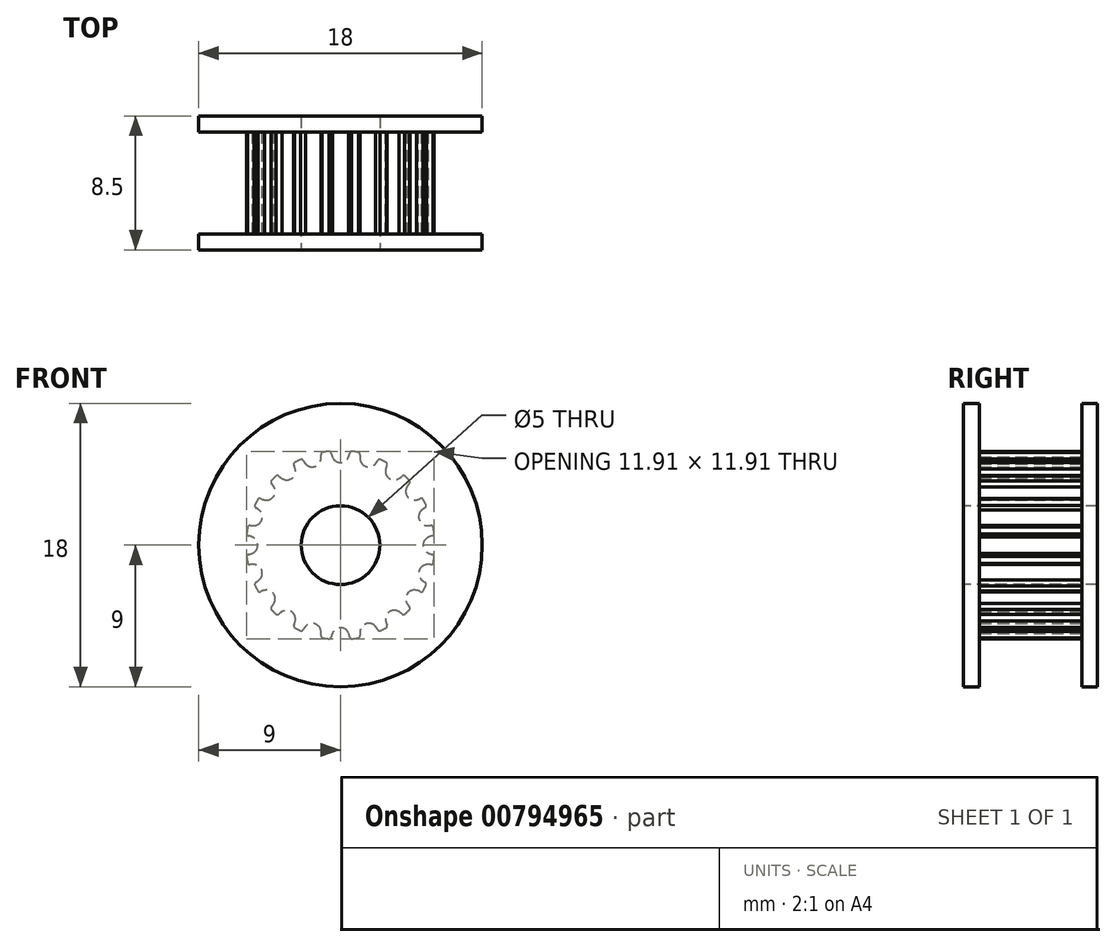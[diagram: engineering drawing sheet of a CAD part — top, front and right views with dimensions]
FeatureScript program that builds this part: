
annotation { "Feature Type Name" : "Feature", "Feature Type Description" : "" }
export const myFeature = defineFeature(function(context is Context, id is Id, definition is map)
    precondition{}
    {
        {
            var Q0;
            Q0=qCreatedBy(makeId("Front.planeOp"),FACE);
            var sketch = newSketch(context, id + "F0", { "sketchPlane" : qUnion([Q0])});
            skLineSegment(sketch, "E0", {"start": v(-19.17, 17.78) * mm, "end": v(-18.17, 17.78) * mm});
            skLineSegment(sketch, "E1", {"start": v(-18.17, 17.78) * mm, "end": v(-18.17, 18.4) * mm});
            skArc(sketch, "E2", {"start": v(-18.67, 18.85) * mm, "mid": v(-18.88, 19.07) * mm, "end": v(-19.17, 19.16) * mm});
            skArc(sketch, "E3", {"start": v(-18.58, 18.54) * mm, "mid": v(-18.61, 18.7) * mm, "end": v(-18.67, 18.85) * mm});
            skArc(sketch, "E4", {"start": v(-18.58, 18.54) * mm, "mid": v(-18.53, 18.44) * mm, "end": v(-18.43, 18.4) * mm});
            skLineSegment(sketch, "E5", {"start": v(-18.43, 18.4) * mm, "end": v(-18.17, 18.4) * mm});
            skArc(sketch, "E6.0.MirrorCS", {"start": v(-19.67, 18.85) * mm, "mid": v(-19.47, 19.07) * mm, "end": v(-19.17, 19.16) * mm});
            skArc(sketch, "E7.0.MirrorCS", {"start": v(-19.76, 18.54) * mm, "mid": v(-19.73, 18.7) * mm, "end": v(-19.67, 18.85) * mm});
            skArc(sketch, "E8.0.MirrorCS", {"start": v(-19.76, 18.54) * mm, "mid": v(-19.81, 18.44) * mm, "end": v(-19.91, 18.4) * mm});
            skLineSegment(sketch, "E9.0.MirrorCS", {"start": v(-19.91, 18.4) * mm, "end": v(-20.17, 18.4) * mm});
            skLineSegment(sketch, "E10.0.MirrorCS", {"start": v(-20.17, 17.78) * mm, "end": v(-20.17, 18.4) * mm});
            skLineSegment(sketch, "E11.0.MirrorCS", {"start": v(-19.17, 17.78) * mm, "end": v(-20.17, 17.78) * mm});
            skLineSegment(sketch, "E12.direction1", {"start": v(-20.17, 17.78) * mm, "end": v(-18.17, 17.78) * mm, "construction": true});
            skLineSegment(sketch, "E13", {"start": v(-20.17, 18.15) * mm, "end": v(-18.17, 18.15) * mm, "construction": true});
            skPoint(sketch, "E14", {"position": v(0, -5.25) * mm});
            skArc(sketch, "E15", {"start": v(0.51, -5.6) * mm, "mid": v(0, -5.25) * mm, "end": v(-0.51, -5.6) * mm});
            skArc(sketch, "E16", {"start": v(-0.51, -5.6) * mm, "mid": v(-0.56, -5.71) * mm, "end": v(-0.59, -5.83) * mm});
            skArc(sketch, "E17", {"start": v(0.59, -5.83) * mm, "mid": v(0.56, -5.71) * mm, "end": v(0.51, -5.6) * mm});
            skArc(sketch, "E18", {"start": v(0.72, -5.96) * mm, "mid": v(0.94, -5.93) * mm, "end": v(1.16, -5.89) * mm});
            skArc(sketch, "E19", {"start": v(0.59, -5.83) * mm, "mid": v(0.66, -5.94) * mm, "end": v(0.8, -5.95) * mm});
            skArc(sketch, "E20", {"start": v(-0.59, -5.83) * mm, "mid": v(-0.66, -5.94) * mm, "end": v(-0.8, -5.95) * mm});
            skArc(sketch, "E21.1.0", {"start": v(2.22, -5.16) * mm, "mid": v(1.62, -5) * mm, "end": v(1.24, -5.48) * mm});
            skPoint(sketch, "E21.1.1", {"position": v(1.62, -5) * mm});
            skArc(sketch, "E21.1.2", {"start": v(1.24, -5.48) * mm, "mid": v(1.23, -5.6) * mm, "end": v(1.24, -5.73) * mm});
            skArc(sketch, "E21.1.3", {"start": v(2.36, -5.37) * mm, "mid": v(2.47, -5.44) * mm, "end": v(2.6, -5.41) * mm});
            skArc(sketch, "E21.1.4", {"start": v(1.24, -5.73) * mm, "mid": v(1.2, -5.85) * mm, "end": v(1.08, -5.9) * mm});
            skArc(sketch, "E21.1.5", {"start": v(2.36, -5.37) * mm, "mid": v(2.3, -5.26) * mm, "end": v(2.22, -5.16) * mm});
            skArc(sketch, "E22.3.2.0", {"start": v(3.7, -4.22) * mm, "mid": v(3.09, -4.25) * mm, "end": v(2.87, -4.83) * mm});
            skPoint(sketch, "E22.4.2.0", {"position": v(3.09, -4.25) * mm});
            skArc(sketch, "E22.5.2.0", {"start": v(2.87, -4.83) * mm, "mid": v(2.9, -4.95) * mm, "end": v(2.95, -5.07) * mm});
            skArc(sketch, "E22.9.2.0", {"start": v(3.9, -4.37) * mm, "mid": v(4.03, -4.41) * mm, "end": v(4.14, -4.35) * mm});
            skArc(sketch, "E22.13.2.0", {"start": v(2.95, -5.07) * mm, "mid": v(2.95, -5.2) * mm, "end": v(2.85, -5.28) * mm});
            skArc(sketch, "E22.17.2.0", {"start": v(3.9, -4.37) * mm, "mid": v(3.81, -4.3) * mm, "end": v(3.7, -4.22) * mm});
            skArc(sketch, "E22.3.3.0", {"start": v(4.83, -2.87) * mm, "mid": v(4.25, -3.09) * mm, "end": v(4.22, -3.7) * mm});
            skPoint(sketch, "E22.4.3.0", {"position": v(4.25, -3.09) * mm});
            skArc(sketch, "E22.5.3.0", {"start": v(4.22, -3.7) * mm, "mid": v(4.3, -3.81) * mm, "end": v(4.37, -3.9) * mm});
            skArc(sketch, "E22.9.3.0", {"start": v(5.07, -2.95) * mm, "mid": v(5.2, -2.95) * mm, "end": v(5.28, -2.85) * mm});
            skArc(sketch, "E22.13.3.0", {"start": v(4.37, -3.9) * mm, "mid": v(4.41, -4.03) * mm, "end": v(4.35, -4.14) * mm});
            skArc(sketch, "E22.17.3.0", {"start": v(5.07, -2.95) * mm, "mid": v(4.95, -2.9) * mm, "end": v(4.83, -2.87) * mm});
            skArc(sketch, "E22.3.4.0", {"start": v(5.48, -1.24) * mm, "mid": v(5, -1.62) * mm, "end": v(5.16, -2.22) * mm});
            skPoint(sketch, "E22.4.4.0", {"position": v(5, -1.62) * mm});
            skArc(sketch, "E22.5.4.0", {"start": v(5.16, -2.22) * mm, "mid": v(5.26, -2.3) * mm, "end": v(5.37, -2.36) * mm});
            skArc(sketch, "E22.9.4.0", {"start": v(5.73, -1.24) * mm, "mid": v(5.85, -1.2) * mm, "end": v(5.9, -1.08) * mm});
            skArc(sketch, "E22.13.4.0", {"start": v(5.37, -2.36) * mm, "mid": v(5.44, -2.47) * mm, "end": v(5.41, -2.6) * mm});
            skArc(sketch, "E22.17.4.0", {"start": v(5.73, -1.24) * mm, "mid": v(5.6, -1.23) * mm, "end": v(5.48, -1.24) * mm});
            skArc(sketch, "E22.3.5.0", {"start": v(5.6, 0.51) * mm, "mid": v(5.25, 0) * mm, "end": v(5.6, -0.51) * mm});
            skPoint(sketch, "E22.4.5.0", {"position": v(5.25, 0) * mm});
            skArc(sketch, "E22.5.5.0", {"start": v(5.6, -0.51) * mm, "mid": v(5.71, -0.56) * mm, "end": v(5.83, -0.59) * mm});
            skArc(sketch, "E22.9.5.0", {"start": v(5.83, 0.59) * mm, "mid": v(5.94, 0.66) * mm, "end": v(5.95, 0.8) * mm});
            skArc(sketch, "E22.13.5.0", {"start": v(5.83, -0.59) * mm, "mid": v(5.94, -0.66) * mm, "end": v(5.95, -0.8) * mm});
            skArc(sketch, "E22.17.5.0", {"start": v(5.83, 0.59) * mm, "mid": v(5.71, 0.56) * mm, "end": v(5.6, 0.51) * mm});
            skArc(sketch, "E22.3.6.0", {"start": v(5.16, 2.22) * mm, "mid": v(5, 1.62) * mm, "end": v(5.48, 1.24) * mm});
            skPoint(sketch, "E22.4.6.0", {"position": v(5, 1.62) * mm});
            skArc(sketch, "E22.5.6.0", {"start": v(5.48, 1.24) * mm, "mid": v(5.6, 1.23) * mm, "end": v(5.73, 1.24) * mm});
            skArc(sketch, "E22.9.6.0", {"start": v(5.37, 2.36) * mm, "mid": v(5.44, 2.47) * mm, "end": v(5.41, 2.6) * mm});
            skArc(sketch, "E22.13.6.0", {"start": v(5.73, 1.24) * mm, "mid": v(5.85, 1.2) * mm, "end": v(5.9, 1.08) * mm});
            skArc(sketch, "E22.17.6.0", {"start": v(5.37, 2.36) * mm, "mid": v(5.26, 2.3) * mm, "end": v(5.16, 2.22) * mm});
            skArc(sketch, "E22.3.7.0", {"start": v(4.22, 3.7) * mm, "mid": v(4.25, 3.09) * mm, "end": v(4.83, 2.87) * mm});
            skPoint(sketch, "E22.4.7.0", {"position": v(4.25, 3.09) * mm});
            skArc(sketch, "E22.5.7.0", {"start": v(4.83, 2.87) * mm, "mid": v(4.95, 2.9) * mm, "end": v(5.07, 2.95) * mm});
            skArc(sketch, "E22.9.7.0", {"start": v(4.37, 3.9) * mm, "mid": v(4.41, 4.03) * mm, "end": v(4.35, 4.14) * mm});
            skArc(sketch, "E22.13.7.0", {"start": v(5.07, 2.95) * mm, "mid": v(5.2, 2.95) * mm, "end": v(5.28, 2.85) * mm});
            skArc(sketch, "E22.17.7.0", {"start": v(4.37, 3.9) * mm, "mid": v(4.3, 3.81) * mm, "end": v(4.22, 3.7) * mm});
            skArc(sketch, "E22.3.8.0", {"start": v(2.87, 4.83) * mm, "mid": v(3.09, 4.25) * mm, "end": v(3.7, 4.22) * mm});
            skPoint(sketch, "E22.4.8.0", {"position": v(3.09, 4.25) * mm});
            skArc(sketch, "E22.5.8.0", {"start": v(3.7, 4.22) * mm, "mid": v(3.81, 4.3) * mm, "end": v(3.9, 4.37) * mm});
            skArc(sketch, "E22.9.8.0", {"start": v(2.95, 5.07) * mm, "mid": v(2.95, 5.2) * mm, "end": v(2.85, 5.28) * mm});
            skArc(sketch, "E22.13.8.0", {"start": v(3.9, 4.37) * mm, "mid": v(4.03, 4.41) * mm, "end": v(4.14, 4.35) * mm});
            skArc(sketch, "E22.17.8.0", {"start": v(2.95, 5.07) * mm, "mid": v(2.9, 4.95) * mm, "end": v(2.87, 4.83) * mm});
            skArc(sketch, "E22.3.9.0", {"start": v(1.24, 5.48) * mm, "mid": v(1.62, 5) * mm, "end": v(2.22, 5.16) * mm});
            skPoint(sketch, "E22.4.9.0", {"position": v(1.62, 5) * mm});
            skArc(sketch, "E22.5.9.0", {"start": v(2.22, 5.16) * mm, "mid": v(2.3, 5.26) * mm, "end": v(2.36, 5.37) * mm});
            skArc(sketch, "E22.9.9.0", {"start": v(1.24, 5.73) * mm, "mid": v(1.2, 5.85) * mm, "end": v(1.08, 5.9) * mm});
            skArc(sketch, "E22.13.9.0", {"start": v(2.36, 5.37) * mm, "mid": v(2.47, 5.44) * mm, "end": v(2.6, 5.41) * mm});
            skArc(sketch, "E22.17.9.0", {"start": v(1.24, 5.73) * mm, "mid": v(1.23, 5.6) * mm, "end": v(1.24, 5.48) * mm});
            skArc(sketch, "E22.3.10.0", {"start": v(-0.51, 5.6) * mm, "mid": v(0, 5.25) * mm, "end": v(0.51, 5.6) * mm});
            skPoint(sketch, "E22.4.10.0", {"position": v(0, 5.25) * mm});
            skArc(sketch, "E22.5.10.0", {"start": v(0.51, 5.6) * mm, "mid": v(0.56, 5.71) * mm, "end": v(0.59, 5.83) * mm});
            skArc(sketch, "E22.9.10.0", {"start": v(-0.59, 5.83) * mm, "mid": v(-0.66, 5.94) * mm, "end": v(-0.8, 5.95) * mm});
            skArc(sketch, "E22.13.10.0", {"start": v(0.59, 5.83) * mm, "mid": v(0.66, 5.94) * mm, "end": v(0.8, 5.95) * mm});
            skArc(sketch, "E22.17.10.0", {"start": v(-0.59, 5.83) * mm, "mid": v(-0.56, 5.71) * mm, "end": v(-0.51, 5.6) * mm});
            skArc(sketch, "E22.3.11.0", {"start": v(-2.22, 5.16) * mm, "mid": v(-1.62, 5) * mm, "end": v(-1.24, 5.48) * mm});
            skPoint(sketch, "E22.4.11.0", {"position": v(-1.62, 5) * mm});
            skArc(sketch, "E22.5.11.0", {"start": v(-1.24, 5.48) * mm, "mid": v(-1.23, 5.6) * mm, "end": v(-1.24, 5.73) * mm});
            skArc(sketch, "E22.9.11.0", {"start": v(-2.36, 5.37) * mm, "mid": v(-2.47, 5.44) * mm, "end": v(-2.6, 5.41) * mm});
            skArc(sketch, "E22.13.11.0", {"start": v(-1.24, 5.73) * mm, "mid": v(-1.2, 5.85) * mm, "end": v(-1.08, 5.9) * mm});
            skArc(sketch, "E22.17.11.0", {"start": v(-2.36, 5.37) * mm, "mid": v(-2.3, 5.26) * mm, "end": v(-2.22, 5.16) * mm});
            skArc(sketch, "E22.3.12.0", {"start": v(-3.7, 4.22) * mm, "mid": v(-3.09, 4.25) * mm, "end": v(-2.87, 4.83) * mm});
            skPoint(sketch, "E22.4.12.0", {"position": v(-3.09, 4.25) * mm});
            skArc(sketch, "E22.5.12.0", {"start": v(-2.87, 4.83) * mm, "mid": v(-2.9, 4.95) * mm, "end": v(-2.95, 5.07) * mm});
            skArc(sketch, "E22.9.12.0", {"start": v(-3.9, 4.37) * mm, "mid": v(-4.03, 4.41) * mm, "end": v(-4.14, 4.35) * mm});
            skArc(sketch, "E22.13.12.0", {"start": v(-2.95, 5.07) * mm, "mid": v(-2.95, 5.2) * mm, "end": v(-2.85, 5.28) * mm});
            skArc(sketch, "E22.17.12.0", {"start": v(-3.9, 4.37) * mm, "mid": v(-3.81, 4.3) * mm, "end": v(-3.7, 4.22) * mm});
            skArc(sketch, "E22.3.13.0", {"start": v(-4.83, 2.87) * mm, "mid": v(-4.25, 3.09) * mm, "end": v(-4.22, 3.7) * mm});
            skPoint(sketch, "E22.4.13.0", {"position": v(-4.25, 3.09) * mm});
            skArc(sketch, "E22.5.13.0", {"start": v(-4.22, 3.7) * mm, "mid": v(-4.3, 3.81) * mm, "end": v(-4.37, 3.9) * mm});
            skArc(sketch, "E22.9.13.0", {"start": v(-5.07, 2.95) * mm, "mid": v(-5.2, 2.95) * mm, "end": v(-5.28, 2.85) * mm});
            skArc(sketch, "E22.13.13.0", {"start": v(-4.37, 3.9) * mm, "mid": v(-4.41, 4.03) * mm, "end": v(-4.35, 4.14) * mm});
            skArc(sketch, "E22.17.13.0", {"start": v(-5.07, 2.95) * mm, "mid": v(-4.95, 2.9) * mm, "end": v(-4.83, 2.87) * mm});
            skArc(sketch, "E22.3.14.0", {"start": v(-5.48, 1.24) * mm, "mid": v(-5, 1.62) * mm, "end": v(-5.16, 2.22) * mm});
            skPoint(sketch, "E22.4.14.0", {"position": v(-5, 1.62) * mm});
            skArc(sketch, "E22.5.14.0", {"start": v(-5.16, 2.22) * mm, "mid": v(-5.26, 2.3) * mm, "end": v(-5.37, 2.36) * mm});
            skArc(sketch, "E22.9.14.0", {"start": v(-5.73, 1.24) * mm, "mid": v(-5.85, 1.2) * mm, "end": v(-5.9, 1.08) * mm});
            skArc(sketch, "E22.13.14.0", {"start": v(-5.37, 2.36) * mm, "mid": v(-5.44, 2.47) * mm, "end": v(-5.41, 2.6) * mm});
            skArc(sketch, "E22.17.14.0", {"start": v(-5.73, 1.24) * mm, "mid": v(-5.6, 1.23) * mm, "end": v(-5.48, 1.24) * mm});
            skArc(sketch, "E22.3.15.0", {"start": v(-5.6, -0.51) * mm, "mid": v(-5.25, 0) * mm, "end": v(-5.6, 0.51) * mm});
            skPoint(sketch, "E22.4.15.0", {"position": v(-5.25, 0) * mm});
            skArc(sketch, "E22.5.15.0", {"start": v(-5.6, 0.51) * mm, "mid": v(-5.71, 0.56) * mm, "end": v(-5.83, 0.59) * mm});
            skArc(sketch, "E22.9.15.0", {"start": v(-5.83, -0.59) * mm, "mid": v(-5.94, -0.66) * mm, "end": v(-5.95, -0.8) * mm});
            skArc(sketch, "E22.13.15.0", {"start": v(-5.83, 0.59) * mm, "mid": v(-5.94, 0.66) * mm, "end": v(-5.95, 0.8) * mm});
            skArc(sketch, "E22.17.15.0", {"start": v(-5.83, -0.59) * mm, "mid": v(-5.71, -0.56) * mm, "end": v(-5.6, -0.51) * mm});
            skArc(sketch, "E22.3.16.0", {"start": v(-5.16, -2.22) * mm, "mid": v(-5, -1.62) * mm, "end": v(-5.48, -1.24) * mm});
            skPoint(sketch, "E22.4.16.0", {"position": v(-5, -1.62) * mm});
            skArc(sketch, "E22.5.16.0", {"start": v(-5.48, -1.24) * mm, "mid": v(-5.6, -1.23) * mm, "end": v(-5.73, -1.24) * mm});
            skArc(sketch, "E22.9.16.0", {"start": v(-5.37, -2.36) * mm, "mid": v(-5.44, -2.47) * mm, "end": v(-5.41, -2.6) * mm});
            skArc(sketch, "E22.13.16.0", {"start": v(-5.73, -1.24) * mm, "mid": v(-5.85, -1.2) * mm, "end": v(-5.9, -1.08) * mm});
            skArc(sketch, "E22.17.16.0", {"start": v(-5.37, -2.36) * mm, "mid": v(-5.26, -2.3) * mm, "end": v(-5.16, -2.22) * mm});
            skArc(sketch, "E22.3.17.0", {"start": v(-4.22, -3.7) * mm, "mid": v(-4.25, -3.09) * mm, "end": v(-4.83, -2.87) * mm});
            skPoint(sketch, "E22.4.17.0", {"position": v(-4.25, -3.09) * mm});
            skArc(sketch, "E22.5.17.0", {"start": v(-4.83, -2.87) * mm, "mid": v(-4.95, -2.9) * mm, "end": v(-5.07, -2.95) * mm});
            skArc(sketch, "E22.9.17.0", {"start": v(-4.37, -3.9) * mm, "mid": v(-4.41, -4.03) * mm, "end": v(-4.35, -4.14) * mm});
            skArc(sketch, "E22.13.17.0", {"start": v(-5.07, -2.95) * mm, "mid": v(-5.2, -2.95) * mm, "end": v(-5.28, -2.85) * mm});
            skArc(sketch, "E22.17.17.0", {"start": v(-4.37, -3.9) * mm, "mid": v(-4.3, -3.81) * mm, "end": v(-4.22, -3.7) * mm});
            skArc(sketch, "E22.3.18.0", {"start": v(-2.87, -4.83) * mm, "mid": v(-3.09, -4.25) * mm, "end": v(-3.7, -4.22) * mm});
            skPoint(sketch, "E22.4.18.0", {"position": v(-3.09, -4.25) * mm});
            skArc(sketch, "E22.5.18.0", {"start": v(-3.7, -4.22) * mm, "mid": v(-3.81, -4.3) * mm, "end": v(-3.9, -4.37) * mm});
            skArc(sketch, "E22.9.18.0", {"start": v(-2.95, -5.07) * mm, "mid": v(-2.95, -5.2) * mm, "end": v(-2.85, -5.28) * mm});
            skArc(sketch, "E22.13.18.0", {"start": v(-3.9, -4.37) * mm, "mid": v(-4.03, -4.41) * mm, "end": v(-4.14, -4.35) * mm});
            skArc(sketch, "E22.17.18.0", {"start": v(-2.95, -5.07) * mm, "mid": v(-2.9, -4.95) * mm, "end": v(-2.87, -4.83) * mm});
            skArc(sketch, "E22.3.19.0", {"start": v(-1.24, -5.48) * mm, "mid": v(-1.62, -5) * mm, "end": v(-2.22, -5.16) * mm});
            skPoint(sketch, "E22.4.19.0", {"position": v(-1.62, -5) * mm});
            skArc(sketch, "E22.5.19.0", {"start": v(-2.22, -5.16) * mm, "mid": v(-2.3, -5.26) * mm, "end": v(-2.36, -5.37) * mm});
            skArc(sketch, "E22.9.19.0", {"start": v(-1.24, -5.73) * mm, "mid": v(-1.2, -5.85) * mm, "end": v(-1.08, -5.9) * mm});
            skArc(sketch, "E22.13.19.0", {"start": v(-2.36, -5.37) * mm, "mid": v(-2.47, -5.44) * mm, "end": v(-2.6, -5.41) * mm});
            skArc(sketch, "E22.17.19.0", {"start": v(-1.24, -5.73) * mm, "mid": v(-1.23, -5.6) * mm, "end": v(-1.24, -5.48) * mm});
            skArc(sketch, "E23.trimOffspring", {"start": v(2.52, -5.44) * mm, "mid": v(2.72, -5.35) * mm, "end": v(2.92, -5.24) * mm});
            skArc(sketch, "E24.trimOffspring", {"start": v(4.08, -4.4) * mm, "mid": v(4.24, -4.24) * mm, "end": v(4.4, -4.08) * mm});
            skArc(sketch, "E25.trimOffspring", {"start": v(5.24, -2.92) * mm, "mid": v(5.33, -2.76) * mm, "end": v(5.41, -2.6) * mm});
            skArc(sketch, "E26.trimOffspring", {"start": v(5.89, -1.16) * mm, "mid": v(5.93, -0.94) * mm, "end": v(5.96, -0.72) * mm});
            skArc(sketch, "E27.trimOffspring", {"start": v(5.44, 2.52) * mm, "mid": v(5.35, 2.72) * mm, "end": v(5.24, 2.92) * mm});
            skArc(sketch, "E28.trimOffspring", {"start": v(4.4, 4.08) * mm, "mid": v(4.24, 4.24) * mm, "end": v(4.08, 4.4) * mm});
            skArc(sketch, "E29.trimOffspring", {"start": v(5.96, 0.72) * mm, "mid": v(5.93, 0.94) * mm, "end": v(5.89, 1.16) * mm});
            skArc(sketch, "E30.trimOffspring", {"start": v(2.92, 5.24) * mm, "mid": v(2.72, 5.35) * mm, "end": v(2.52, 5.44) * mm});
            skArc(sketch, "E31.trimOffspring", {"start": v(1.16, 5.89) * mm, "mid": v(0.94, 5.93) * mm, "end": v(0.72, 5.96) * mm});
            skArc(sketch, "E32.trimOffspring", {"start": v(-0.72, 5.96) * mm, "mid": v(-0.94, 5.93) * mm, "end": v(-1.16, 5.89) * mm});
            skArc(sketch, "E33.trimOffspring", {"start": v(-2.52, 5.44) * mm, "mid": v(-2.72, 5.35) * mm, "end": v(-2.92, 5.24) * mm});
            skArc(sketch, "E34.trimOffspring", {"start": v(-4.08, 4.4) * mm, "mid": v(-4.24, 4.24) * mm, "end": v(-4.4, 4.08) * mm});
            skArc(sketch, "E35.trimOffspring", {"start": v(-5.24, 2.92) * mm, "mid": v(-5.35, 2.72) * mm, "end": v(-5.44, 2.52) * mm});
            skArc(sketch, "E36.trimOffspring", {"start": v(-5.89, 1.16) * mm, "mid": v(-5.93, 0.94) * mm, "end": v(-5.96, 0.72) * mm});
            skArc(sketch, "E37.trimOffspring", {"start": v(-5.96, -0.72) * mm, "mid": v(-5.93, -0.94) * mm, "end": v(-5.89, -1.16) * mm});
            skArc(sketch, "E38.trimOffspring", {"start": v(-5.44, -2.52) * mm, "mid": v(-5.35, -2.72) * mm, "end": v(-5.24, -2.92) * mm});
            skArc(sketch, "E39.trimOffspring", {"start": v(-4.4, -4.08) * mm, "mid": v(-4.24, -4.24) * mm, "end": v(-4.08, -4.4) * mm});
            skArc(sketch, "E40.trimOffspring", {"start": v(-2.92, -5.24) * mm, "mid": v(-2.72, -5.35) * mm, "end": v(-2.52, -5.44) * mm});
            skArc(sketch, "E41.trimOffspring", {"start": v(-1.16, -5.89) * mm, "mid": v(-0.94, -5.93) * mm, "end": v(-0.72, -5.96) * mm});
            skSolve(sketch);
        }
        {
            var Q0;
            Q0=makeQuery(id+"F0.imprint","IMPRINT",FACE,{"disambiguationData":[TD([[makeQuery(id+"F0.imprint","IMPRINT",EDGE,{"derivedFrom":sQuery(id+"F0.wireOp",EDGE,"E15")}),-1.0]])]});
            extrude(context, id + "F1", {"entities" : qUnion([Q0]), "endBound" : BoundingType.SYMMETRIC, "depth" : 6.5 * mm, "offsetDistance" : 25 * mm});
        }
        {
            var Q0;
            Q0=makeQuery(id+"F1.opExtrude","CAP_FACE",FACE,{"disambiguationData":[OSD([sQuery(id+"F0.wireOp",EDGE,"E15"),sQuery(id+"F0.wireOp",EDGE,"E16"),sQuery(id+"F0.wireOp",EDGE,"E17"),sQuery(id+"F0.wireOp",EDGE,"E18"),sQuery(id+"F0.wireOp",EDGE,"E19"),sQuery(id+"F0.wireOp",EDGE,"E20"),sQuery(id+"F0.wireOp",EDGE,"E21.1.0"),sQuery(id+"F0.wireOp",EDGE,"E21.1.2"),sQuery(id+"F0.wireOp",EDGE,"E21.1.3"),sQuery(id+"F0.wireOp",EDGE,"E21.1.4"),sQuery(id+"F0.wireOp",EDGE,"E21.1.5"),sQuery(id+"F0.wireOp",EDGE,"E22.3.2.0"),sQuery(id+"F0.wireOp",EDGE,"E22.5.2.0"),sQuery(id+"F0.wireOp",EDGE,"E22.9.2.0"),sQuery(id+"F0.wireOp",EDGE,"E22.13.2.0"),sQuery(id+"F0.wireOp",EDGE,"E22.17.2.0"),sQuery(id+"F0.wireOp",EDGE,"E22.3.3.0"),sQuery(id+"F0.wireOp",EDGE,"E22.5.3.0"),sQuery(id+"F0.wireOp",EDGE,"E22.9.3.0"),sQuery(id+"F0.wireOp",EDGE,"E22.13.3.0"),sQuery(id+"F0.wireOp",EDGE,"E22.17.3.0"),sQuery(id+"F0.wireOp",EDGE,"E22.3.4.0"),sQuery(id+"F0.wireOp",EDGE,"E22.5.4.0"),sQuery(id+"F0.wireOp",EDGE,"E22.9.4.0"),sQuery(id+"F0.wireOp",EDGE,"E22.13.4.0"),sQuery(id+"F0.wireOp",EDGE,"E22.17.4.0"),sQuery(id+"F0.wireOp",EDGE,"E22.3.5.0"),sQuery(id+"F0.wireOp",EDGE,"E22.5.5.0"),sQuery(id+"F0.wireOp",EDGE,"E22.9.5.0"),sQuery(id+"F0.wireOp",EDGE,"E22.13.5.0"),sQuery(id+"F0.wireOp",EDGE,"E22.17.5.0"),sQuery(id+"F0.wireOp",EDGE,"E22.3.6.0"),sQuery(id+"F0.wireOp",EDGE,"E22.5.6.0"),sQuery(id+"F0.wireOp",EDGE,"E22.9.6.0"),sQuery(id+"F0.wireOp",EDGE,"E22.13.6.0"),sQuery(id+"F0.wireOp",EDGE,"E22.17.6.0"),sQuery(id+"F0.wireOp",EDGE,"E22.3.7.0"),sQuery(id+"F0.wireOp",EDGE,"E22.5.7.0"),sQuery(id+"F0.wireOp",EDGE,"E22.9.7.0"),sQuery(id+"F0.wireOp",EDGE,"E22.13.7.0"),sQuery(id+"F0.wireOp",EDGE,"E22.17.7.0"),sQuery(id+"F0.wireOp",EDGE,"E22.3.8.0"),sQuery(id+"F0.wireOp",EDGE,"E22.5.8.0"),sQuery(id+"F0.wireOp",EDGE,"E22.9.8.0"),sQuery(id+"F0.wireOp",EDGE,"E22.13.8.0"),sQuery(id+"F0.wireOp",EDGE,"E22.17.8.0"),sQuery(id+"F0.wireOp",EDGE,"E22.3.9.0"),sQuery(id+"F0.wireOp",EDGE,"E22.5.9.0"),sQuery(id+"F0.wireOp",EDGE,"E22.9.9.0"),sQuery(id+"F0.wireOp",EDGE,"E22.13.9.0"),sQuery(id+"F0.wireOp",EDGE,"E22.17.9.0"),sQuery(id+"F0.wireOp",EDGE,"E22.3.10.0"),sQuery(id+"F0.wireOp",EDGE,"E22.5.10.0"),sQuery(id+"F0.wireOp",EDGE,"E22.9.10.0"),sQuery(id+"F0.wireOp",EDGE,"E22.13.10.0"),sQuery(id+"F0.wireOp",EDGE,"E22.17.10.0"),sQuery(id+"F0.wireOp",EDGE,"E22.3.11.0"),sQuery(id+"F0.wireOp",EDGE,"E22.5.11.0"),sQuery(id+"F0.wireOp",EDGE,"E22.9.11.0"),sQuery(id+"F0.wireOp",EDGE,"E22.13.11.0"),sQuery(id+"F0.wireOp",EDGE,"E22.17.11.0"),sQuery(id+"F0.wireOp",EDGE,"E22.3.12.0"),sQuery(id+"F0.wireOp",EDGE,"E22.5.12.0"),sQuery(id+"F0.wireOp",EDGE,"E22.9.12.0"),sQuery(id+"F0.wireOp",EDGE,"E22.13.12.0"),sQuery(id+"F0.wireOp",EDGE,"E22.17.12.0"),sQuery(id+"F0.wireOp",EDGE,"E22.3.13.0"),sQuery(id+"F0.wireOp",EDGE,"E22.5.13.0"),sQuery(id+"F0.wireOp",EDGE,"E22.9.13.0"),sQuery(id+"F0.wireOp",EDGE,"E22.13.13.0"),sQuery(id+"F0.wireOp",EDGE,"E22.17.13.0"),sQuery(id+"F0.wireOp",EDGE,"E22.3.14.0"),sQuery(id+"F0.wireOp",EDGE,"E22.5.14.0"),sQuery(id+"F0.wireOp",EDGE,"E22.9.14.0"),sQuery(id+"F0.wireOp",EDGE,"E22.13.14.0"),sQuery(id+"F0.wireOp",EDGE,"E22.17.14.0"),sQuery(id+"F0.wireOp",EDGE,"E22.3.15.0"),sQuery(id+"F0.wireOp",EDGE,"E22.5.15.0"),sQuery(id+"F0.wireOp",EDGE,"E22.9.15.0"),sQuery(id+"F0.wireOp",EDGE,"E22.13.15.0"),sQuery(id+"F0.wireOp",EDGE,"E22.17.15.0"),sQuery(id+"F0.wireOp",EDGE,"E22.3.16.0"),sQuery(id+"F0.wireOp",EDGE,"E22.5.16.0"),sQuery(id+"F0.wireOp",EDGE,"E22.9.16.0"),sQuery(id+"F0.wireOp",EDGE,"E22.13.16.0"),sQuery(id+"F0.wireOp",EDGE,"E22.17.16.0"),sQuery(id+"F0.wireOp",EDGE,"E22.3.17.0"),sQuery(id+"F0.wireOp",EDGE,"E22.5.17.0"),sQuery(id+"F0.wireOp",EDGE,"E22.9.17.0"),sQuery(id+"F0.wireOp",EDGE,"E22.13.17.0"),sQuery(id+"F0.wireOp",EDGE,"E22.17.17.0"),sQuery(id+"F0.wireOp",EDGE,"E22.3.18.0"),sQuery(id+"F0.wireOp",EDGE,"E22.5.18.0"),sQuery(id+"F0.wireOp",EDGE,"E22.9.18.0"),sQuery(id+"F0.wireOp",EDGE,"E22.13.18.0"),sQuery(id+"F0.wireOp",EDGE,"E22.17.18.0"),sQuery(id+"F0.wireOp",EDGE,"E22.3.19.0"),sQuery(id+"F0.wireOp",EDGE,"E22.5.19.0"),sQuery(id+"F0.wireOp",EDGE,"E22.9.19.0"),sQuery(id+"F0.wireOp",EDGE,"E22.13.19.0"),sQuery(id+"F0.wireOp",EDGE,"E22.17.19.0"),sQuery(id+"F0.wireOp",EDGE,"E23.trimOffspring"),sQuery(id+"F0.wireOp",EDGE,"E24.trimOffspring"),sQuery(id+"F0.wireOp",EDGE,"E25.trimOffspring"),sQuery(id+"F0.wireOp",EDGE,"E26.trimOffspring"),sQuery(id+"F0.wireOp",EDGE,"E27.trimOffspring"),sQuery(id+"F0.wireOp",EDGE,"E28.trimOffspring"),sQuery(id+"F0.wireOp",EDGE,"E29.trimOffspring"),sQuery(id+"F0.wireOp",EDGE,"E30.trimOffspring"),sQuery(id+"F0.wireOp",EDGE,"E31.trimOffspring"),sQuery(id+"F0.wireOp",EDGE,"E32.trimOffspring"),sQuery(id+"F0.wireOp",EDGE,"E33.trimOffspring"),sQuery(id+"F0.wireOp",EDGE,"E34.trimOffspring"),sQuery(id+"F0.wireOp",EDGE,"E35.trimOffspring"),sQuery(id+"F0.wireOp",EDGE,"E36.trimOffspring"),sQuery(id+"F0.wireOp",EDGE,"E37.trimOffspring"),sQuery(id+"F0.wireOp",EDGE,"E38.trimOffspring"),sQuery(id+"F0.wireOp",EDGE,"E39.trimOffspring"),sQuery(id+"F0.wireOp",EDGE,"E40.trimOffspring"),sQuery(id+"F0.wireOp",EDGE,"E41.trimOffspring")])],"isStart":false});
            var sketch = newSketch(context, id + "F2", { "sketchPlane" : qUnion([Q0])});
            skCircle(sketch, "E42", {"center": v(0, 0) * mm, "radius": 9 * mm});
            skSolve(sketch);
        }
        {
            var Q0;
            Q0=qSketchRegion(id+"F2",true);
            extrude(context, id + "F3", {"entities" : qUnion([Q0]), "depth" : 1 * mm, "offsetDistance" : 25 * mm});
        }
        {
            var Q0;
            Q0=makeQuery(id+"F3.opExtrude","SWEPT_BODY",BODY,{"disambiguationData":[OSD([sQuery(id+"F2.wireOp",EDGE,"E42")])]});
            var Q1;
            Q1=qCreatedBy(makeId("Front.planeOp"),FACE);
            mirror(context, id + "F4", {"operationType" : NewBodyOperationType.ADD, "entities" : qUnion([Q0]), "mirrorPlane" : qUnion([Q1])});
        }
        {
            var Q0;
            Q0=makeQuery(id+"F3.opExtrude","CAP_FACE",FACE,{"disambiguationData":[OSD([sQuery(id+"F2.wireOp",EDGE,"E42")])],"isStart":false});
            var sketch = newSketch(context, id + "F5", { "sketchPlane" : qUnion([Q0])});
            skCircle(sketch, "E43", {"center": v(0, 0) * mm, "radius": 2.5 * mm});
            skCircle(sketch, "E44.0", {"center": v(0, 0) * mm, "radius": 9 * mm});
            skSolve(sketch);
        }
        {
            var Q0;
            Q0=makeQuery(id+"F5.imprint","IMPRINT",FACE,{"disambiguationData":[TD([[makeQuery(id+"F5.imprint","IMPRINT",EDGE,{"derivedFrom":sQuery(id+"F5.wireOp",EDGE,"E43")}),1.0]])]});
            extrude(context, id + "F6", {"entities" : qUnion([Q0]), "operationType" : NewBodyOperationType.REMOVE, "endBound" : BoundingType.THROUGH_ALL, "oppositeDirection" : true, "depth" : 25 * mm, "offsetDistance" : 25 * mm});
        }
    });
